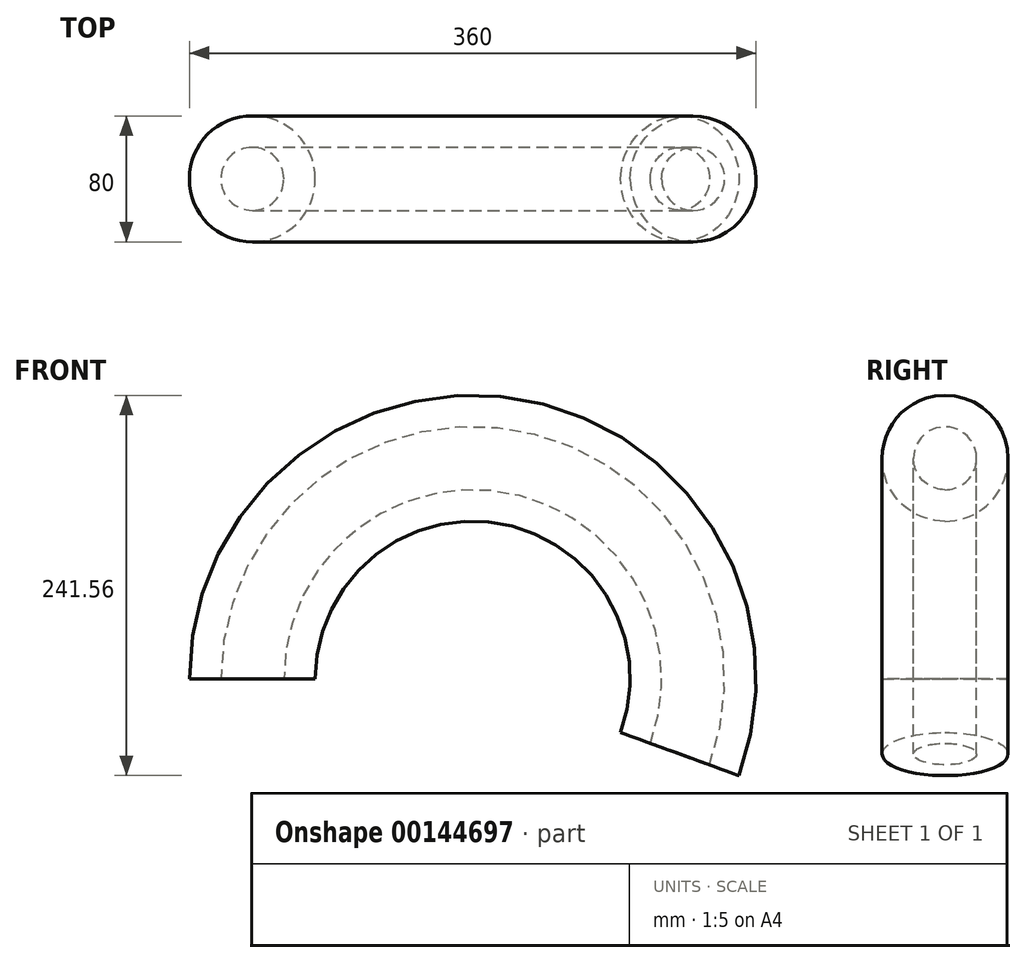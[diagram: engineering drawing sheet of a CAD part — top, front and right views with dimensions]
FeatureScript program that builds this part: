
annotation { "Feature Type Name" : "Feature", "Feature Type Description" : "" }
export const myFeature = defineFeature(function(context is Context, id is Id, definition is map)
    precondition{}
    {
        {
            assignVariable(context, id + "F0", {"name" : "kont", "anyValue" : 200});
        }
        {
            var Q0;
            Q0=qCreatedBy(makeId("Top.planeOp"),FACE);
            var sketch = newSketch(context, id + "F1", { "sketchPlane" : qUnion([Q0])});
            skCircle(sketch, "E0", {"center": v(-140, 0) * mm, "radius": 40 * mm});
            skCircle(sketch, "E1", {"center": v(-140, 0) * mm, "radius": 20 * mm});
            skLineSegment(sketch, "E2", {"start": v(0, 0) * mm, "end": v(0, 41.35) * mm});
            skSolve(sketch);
        }
        {
            var Q0;
            Q0=makeQuery(id+"F1.imprint","IMPRINT",FACE,{"disambiguationData":[TD([[makeQuery(id+"F1.imprint","IMPRINT",EDGE,{"derivedFrom":sQuery(id+"F1.wireOp",EDGE,"E0")}),1.0]])]});
            var Q1;
            Q1=sQuery(id+"F1.wireOp",EDGE,"E2");
            revolve(context, id + "F2", {"entities" : qUnion([Q0]), "axis" : qUnion([Q1]), "revolveType" : RevolveType.ONE_DIRECTION, "angle" : (getVariable(context, 'kont')) * degree});
        }
    });
